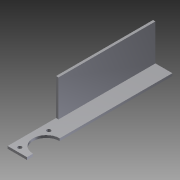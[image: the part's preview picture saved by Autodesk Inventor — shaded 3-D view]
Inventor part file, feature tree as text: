
AUTODESK INVENTOR PART (.ipt)
format: ipt  version: 2012 (Build 160160000, 160)  size: 86,016 bytes
history: native  units: in
note: dims shown in document units (in); Inventor stores cm internally (conversion verified against a paired STEP export)
features: other x3, sketch x2
ambient origin geometry x8: Origin, YZ Plane, XZ Plane, XY Plane, X Axis, Y Axis, Z Axis, Center Point
bodies: Solid1 (feature_tree)
feature tree (5):
  other  "8 ball corner L_MIR.ipt"
  other  "Solid1::8 ball corner L_MIR.ipt"
  sketch  "Sketch1"  dims[d0=0.3937in]
  sketch  "Sketch2"
  other  "TaggingFeature1"
